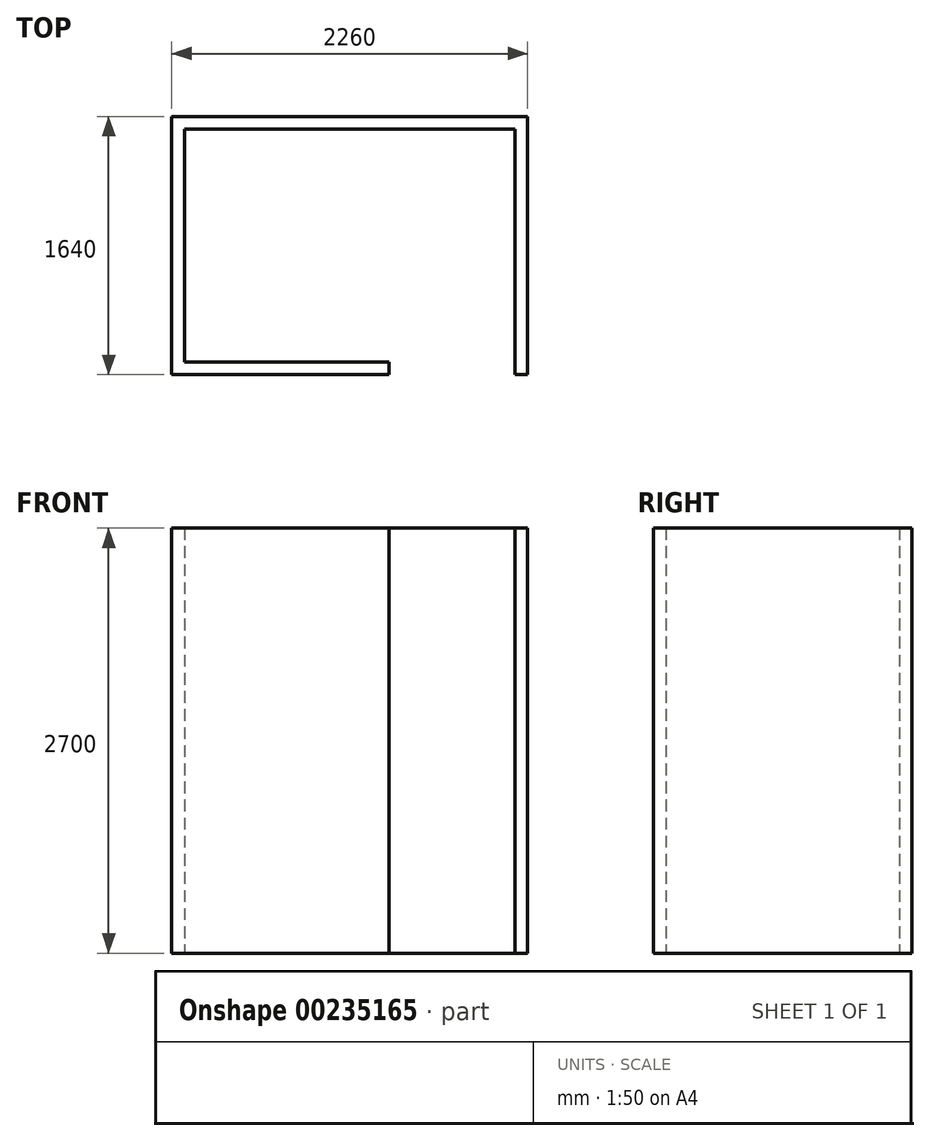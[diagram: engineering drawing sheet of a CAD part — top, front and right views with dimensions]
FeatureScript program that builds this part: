
annotation { "Feature Type Name" : "Feature", "Feature Type Description" : "" }
export const myFeature = defineFeature(function(context is Context, id is Id, definition is map)
    precondition{}
    {
        {
            var Q0;
            Q0=qCreatedBy(makeId("Top.planeOp"),FACE);
            var sketch = newSketch(context, id + "F0", { "sketchPlane" : qUnion([Q0])});
            skLineSegment(sketch, "E0", {"start": v(0, 0) * mm, "end": v(-1380, 0) * mm});
            skLineSegment(sketch, "E1", {"start": v(-1380, 0) * mm, "end": v(-1380, 1640) * mm});
            skLineSegment(sketch, "E2", {"start": v(-1380, 1640) * mm, "end": v(880, 1640) * mm});
            skLineSegment(sketch, "E3", {"start": v(880, 1640) * mm, "end": v(880, 0) * mm});
            skLineSegment(sketch, "E4.0", {"start": v(800, 1560) * mm, "end": v(800, 0) * mm});
            skLineSegment(sketch, "E4.1", {"start": v(-1300, 1560) * mm, "end": v(800, 1560) * mm});
            skLineSegment(sketch, "E4.2", {"start": v(-1300, 80) * mm, "end": v(-1300, 1560) * mm});
            skLineSegment(sketch, "E4.3", {"start": v(0, 80) * mm, "end": v(-1300, 80) * mm});
            skLineSegment(sketch, "E5", {"start": v(0, 80) * mm, "end": v(0, 0) * mm});
            skLineSegment(sketch, "E6", {"start": v(800, 0) * mm, "end": v(880, 0) * mm});
            skSolve(sketch);
        }
        {
            var Q0;
            Q0 = qSketchRegion(id + "F0", true);
            extrude(context, id + "F1", {"entities" : qUnion([Q0]), "depth" : 2700 * mm, "offsetDistance" : 25 * mm});
        }
    });
